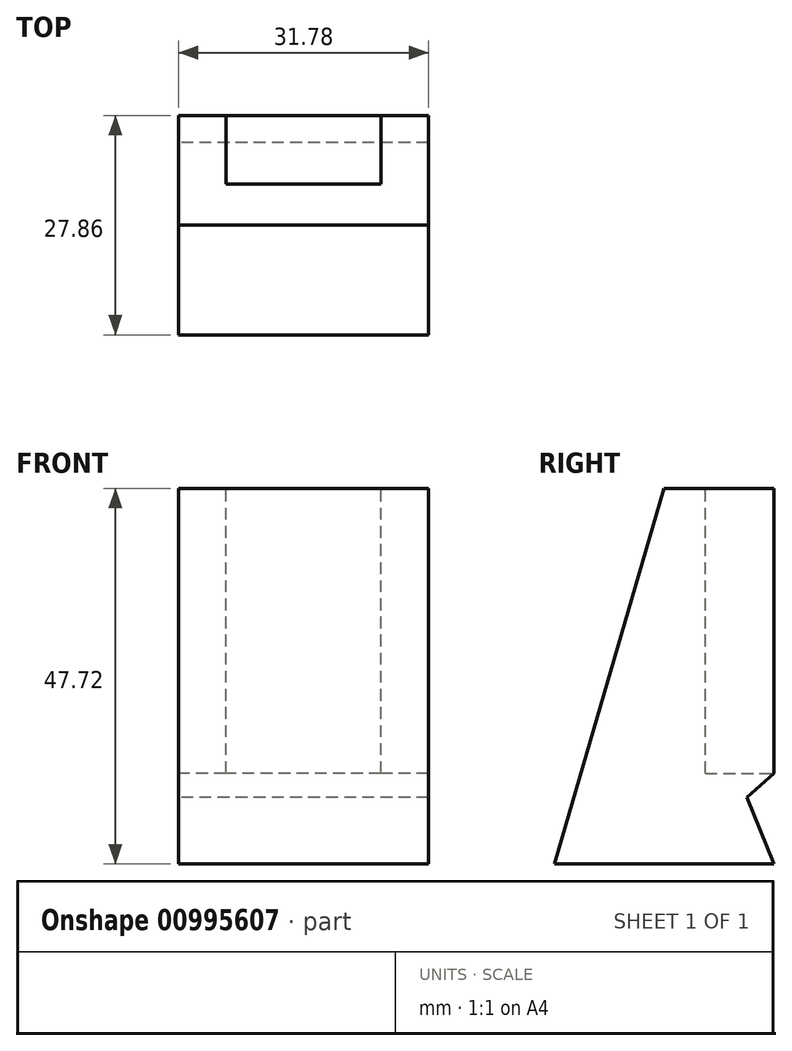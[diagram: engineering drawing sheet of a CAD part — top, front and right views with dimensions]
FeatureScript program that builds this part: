
annotation { "Feature Type Name" : "Feature", "Feature Type Description" : "" }
export const myFeature = defineFeature(function(context is Context, id is Id, definition is map)
    precondition{}
    {
        {
            var Q0;
            Q0=qCreatedBy(makeId("Top.planeOp"),FACE);
            var sketch = newSketch(context, id + "F0", { "sketchPlane" : qUnion([Q0])});
            skLineSegment(sketch, "E0.bottom", {"start": v(15.89, 13.93) * mm, "end": v(-15.89, 13.93) * mm});
            skLineSegment(sketch, "E0.top", {"start": v(15.89, -13.93) * mm, "end": v(-15.89, -13.93) * mm});
            skLineSegment(sketch, "E0.left", {"start": v(15.89, 13.93) * mm, "end": v(15.89, -13.93) * mm});
            skLineSegment(sketch, "E0.right", {"start": v(-15.89, 13.93) * mm, "end": v(-15.89, -13.93) * mm});
            skPoint(sketch, "E0.middle", {"position": v(0, 0) * mm});
            skSolve(sketch);
        }
        {
            var Q0;
            Q0 = qSketchRegion(id + "F0", true);
            extrude(context, id + "F1", {"entities" : qUnion([Q0]), "depth" : 47.72 * mm, "offsetDistance" : 25.4 * mm});
        }
        {
            var Q0;
            Q0=makeQuery(id+"F1.opExtrude","SWEPT_FACE",FACE,{"disambiguationData":[OSD([sQuery(id+"F0.wireOp",EDGE,"E0.right")])]});
            var sketch = newSketch(context, id + "F2", { "sketchPlane" : qUnion([Q0])});
            skLineSegment(sketch, "E1", {"start": v(0, 47.72) * mm, "end": v(13.93, 0) * mm});
            skLineSegment(sketch, "E2", {"start": v(13.93, 0) * mm, "end": v(-13.93, 0) * mm});
            skLineSegment(sketch, "E3", {"start": v(-13.93, 0) * mm, "end": v(-10.5, 8.43) * mm});
            skLineSegment(sketch, "E4", {"start": v(-10.5, 8.43) * mm, "end": v(-10.5, 8.43) * mm});
            skLineSegment(sketch, "E5", {"start": v(-13.93, 11.53) * mm, "end": v(-10.5, 8.43) * mm});
            skLineSegment(sketch, "E6", {"start": v(-13.93, 47.72) * mm, "end": v(-13.93, 0) * mm});
            skLineSegment(sketch, "E7", {"start": v(-13.93, 47.72) * mm, "end": v(0, 47.72) * mm});
            skLineSegment(sketch, "E8", {"start": v(0, 47.72) * mm, "end": v(13.93, 47.72) * mm});
            skLineSegment(sketch, "E9", {"start": v(13.93, 47.72) * mm, "end": v(13.93, 0) * mm});
            skSolve(sketch);
        }
        {
            var Q0;
            Q0=makeQuery(id+"F2.imprint","IMPRINT",FACE,{"disambiguationData":[TD([[makeQuery(id+"F2.imprint","IMPRINT",EDGE,{"derivedFrom":sQuery(id+"F2.wireOp",EDGE,"E1")}),1.0]])]});
            var Q1;
            {var subQ0=sQuery(id+"F2.wireOp",EDGE,"E3");Q1=makeQuery(id+"F2.imprint","IMPRINT",FACE,{"disambiguationData":[TD([[makeQuery(id+"F2.imprint","IMPRINT",EDGE,{"derivedFrom":subQ0}),1.0]])]});}
            extrude(context, id + "F3", {"entities" : qUnion([Q0, Q1]), "operationType" : NewBodyOperationType.REMOVE, "oppositeDirection" : true, "depth" : 35.22 * mm, "offsetDistance" : 25.4 * mm});
        }
        {
            var Q0;
            Q0=makeQuery(id+"F1.opExtrude","SWEPT_FACE",FACE,{"disambiguationData":[OSD([sQuery(id+"F0.wireOp",EDGE,"E0.bottom")])]});
            var sketch = newSketch(context, id + "F4", { "sketchPlane" : qUnion([Q0])});
            skLineSegment(sketch, "E10.bottom", {"start": v(9.85, 11.53) * mm, "end": v(-9.85, 11.53) * mm});
            skLineSegment(sketch, "E10.top", {"start": v(9.85, 48.78) * mm, "end": v(-9.85, 48.78) * mm});
            skLineSegment(sketch, "E10.left", {"start": v(9.85, 11.53) * mm, "end": v(9.85, 48.78) * mm});
            skLineSegment(sketch, "E10.right", {"start": v(-9.85, 11.53) * mm, "end": v(-9.85, 48.78) * mm});
            skPoint(sketch, "E10.middle", {"position": v(0, 30.16) * mm});
            skSolve(sketch);
        }
        {
            var Q0;
            Q0 = qSketchRegion(id + "F4", true);
            extrude(context, id + "F5", {"entities" : qUnion([Q0]), "operationType" : NewBodyOperationType.REMOVE, "oppositeDirection" : true, "depth" : 8.71 * mm, "offsetDistance" : 25.4 * mm});
        }
    });
